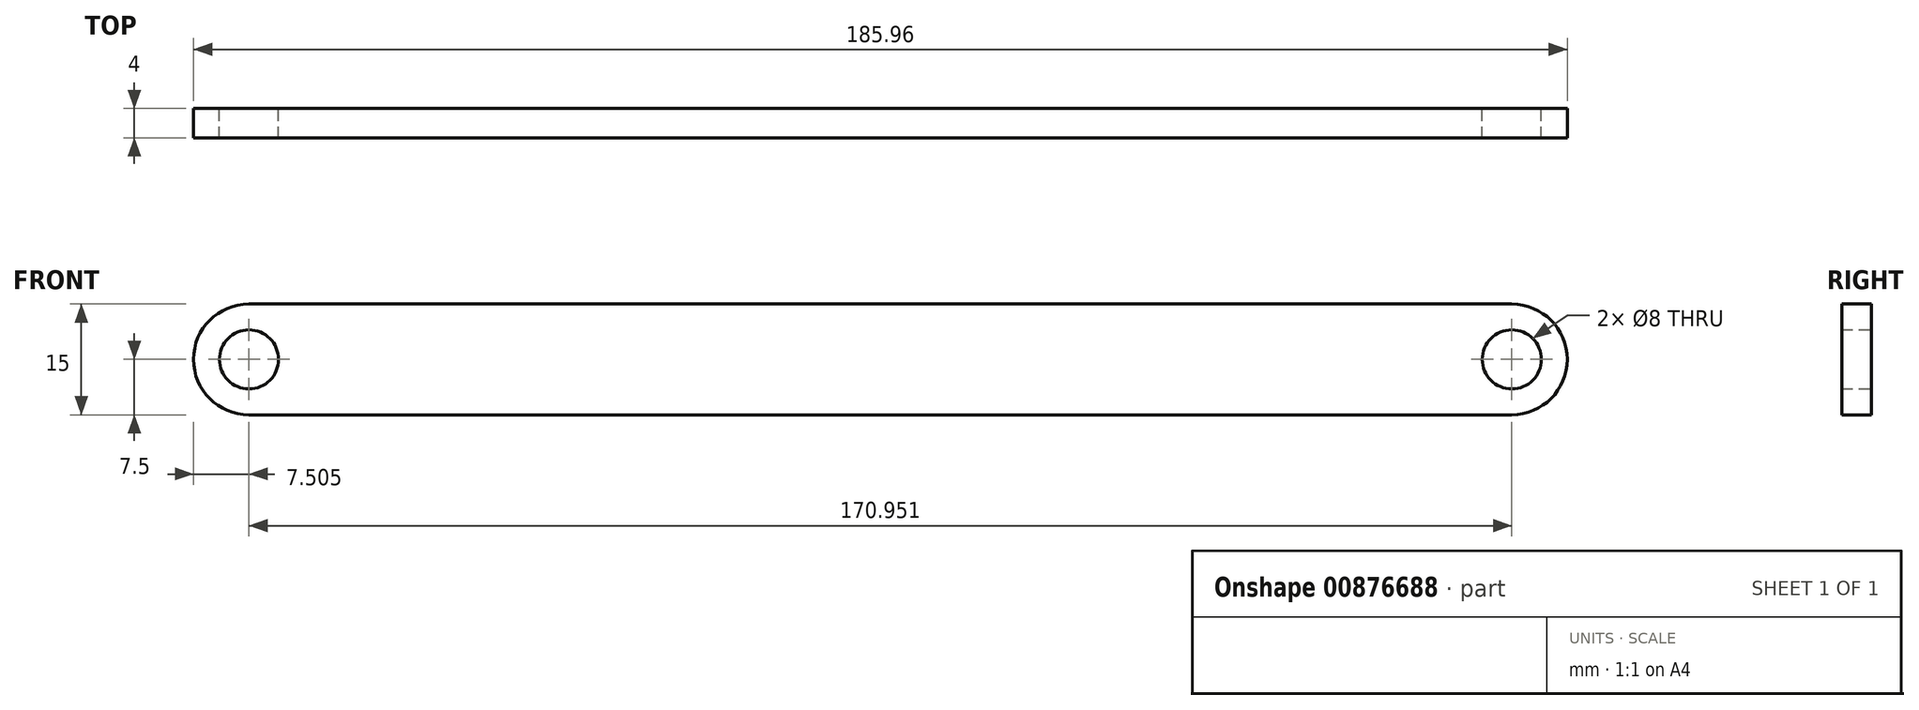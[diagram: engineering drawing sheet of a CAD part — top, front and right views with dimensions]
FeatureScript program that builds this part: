
annotation { "Feature Type Name" : "Feature", "Feature Type Description" : "" }
export const myFeature = defineFeature(function(context is Context, id is Id, definition is map)
    precondition{}
    {
        {
            var Q0;
            Q0=qCreatedBy(makeId("Front.planeOp"),FACE);
            var sketch = newSketch(context, id + "F0", { "sketchPlane" : qUnion([Q0])});
            skCircle(sketch, "E0", {"center": v(85.48, 0) * mm, "radius": 4 * mm});
            skCircle(sketch, "E1", {"center": v(-85.48, 0) * mm, "radius": 4 * mm});
            skArc(sketch, "E2", {"start": v(-85.48, 7.5) * mm, "mid": v(-92.98, 0) * mm, "end": v(-85.48, -7.5) * mm});
            skArc(sketch, "E3", {"start": v(85.48, -7.5) * mm, "mid": v(92.98, 0) * mm, "end": v(85.48, 7.5) * mm});
            skLineSegment(sketch, "E4", {"start": v(-85.48, 7.5) * mm, "end": v(85.48, 7.5) * mm});
            skLineSegment(sketch, "E5", {"start": v(-85.48, -7.5) * mm, "end": v(85.48, -7.5) * mm});
            skSolve(sketch);
        }
        {
            var Q0;
            Q0=makeQuery(id+"F0.imprint","IMPRINT",FACE,{"disambiguationData":[TD([[makeQuery(id+"F0.imprint","IMPRINT",EDGE,{"derivedFrom":sQuery(id+"F0.wireOp",EDGE,"E0")}),-1.0]])]});
            extrude(context, id + "F1", {"entities" : qUnion([Q0]), "depth" : 4 * mm, "offsetDistance" : 25 * mm});
        }
    });
